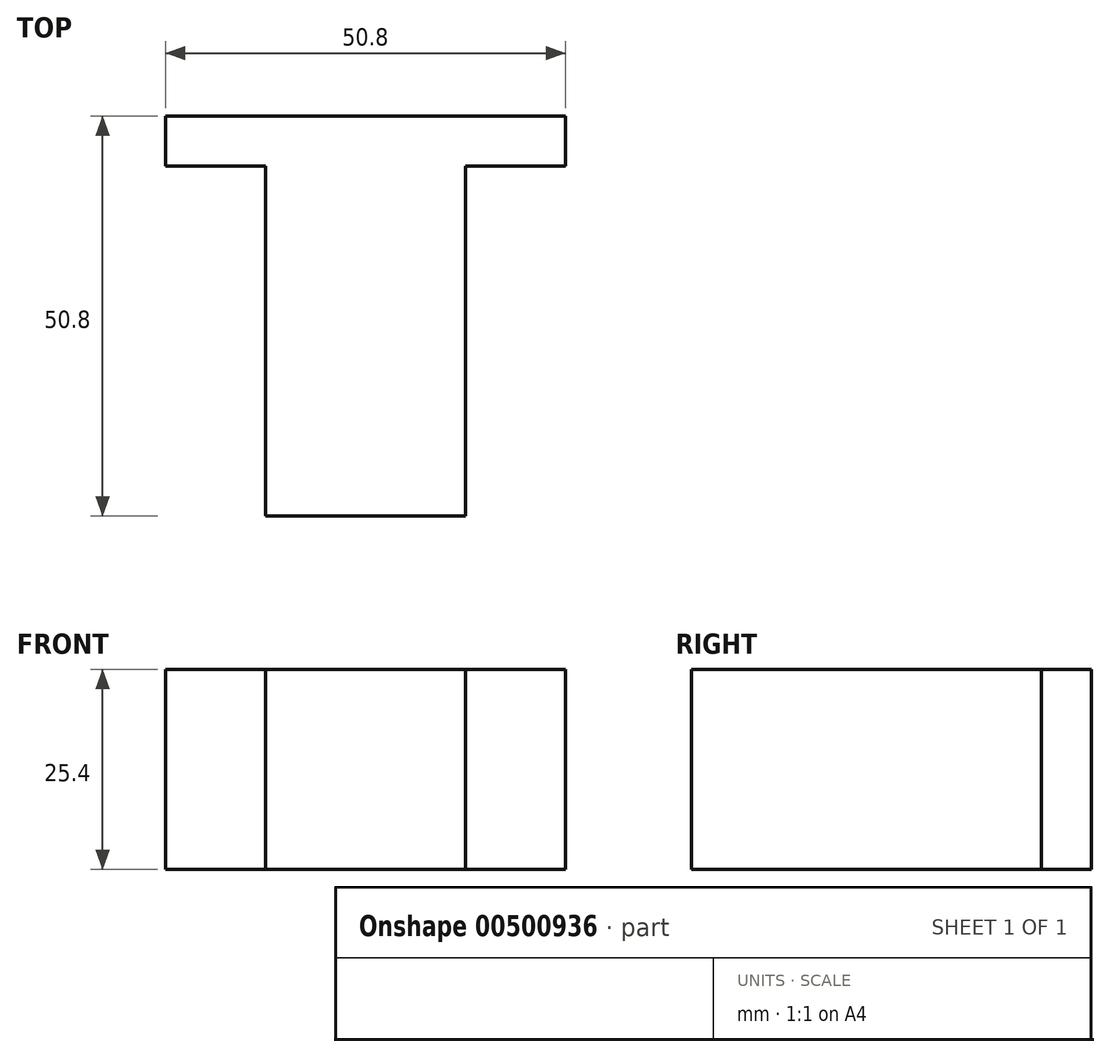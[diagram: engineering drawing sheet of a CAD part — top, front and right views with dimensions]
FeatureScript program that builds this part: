
annotation { "Feature Type Name" : "Feature", "Feature Type Description" : "" }
export const myFeature = defineFeature(function(context is Context, id is Id, definition is map)
    precondition{}
    {
        {
            var Q0;
            Q0=qCreatedBy(makeId("Top.planeOp"),FACE);
            var sketch = newSketch(context, id + "F0", { "sketchPlane" : qUnion([Q0])});
            skLineSegment(sketch, "E0", {"start": v(-30.8, 0) * mm, "end": v(20, 0) * mm});
            skLineSegment(sketch, "E1", {"start": v(20, 0) * mm, "end": v(20, -6.35) * mm});
            skLineSegment(sketch, "E2", {"start": v(20, -6.35) * mm, "end": v(7.3, -6.35) * mm});
            skLineSegment(sketch, "E3", {"start": v(7.3, -6.35) * mm, "end": v(7.3, -50.8) * mm});
            skLineSegment(sketch, "E4", {"start": v(7.3, -50.8) * mm, "end": v(-18.1, -50.8) * mm});
            skLineSegment(sketch, "E5", {"start": v(-18.1, -50.8) * mm, "end": v(-18.1, -6.35) * mm});
            skLineSegment(sketch, "E6", {"start": v(-18.1, -6.35) * mm, "end": v(-30.8, -6.35) * mm});
            skLineSegment(sketch, "E7", {"start": v(-30.8, -6.35) * mm, "end": v(-30.8, 0) * mm});
            skSolve(sketch);
        }
        {
            var Q0;
            Q0=makeQuery(id+"F0.imprint","IMPRINT",FACE,{"disambiguationData":[TD([[makeQuery(id+"F0.imprint","IMPRINT",EDGE,{"derivedFrom":sQuery(id+"F0.wireOp",EDGE,"E0")}),-1.0]])]});
            extrude(context, id + "F1", {"entities" : qUnion([Q0]), "depth" : 25.4 * mm, "offsetDistance" : 25.4 * mm});
        }
    });
